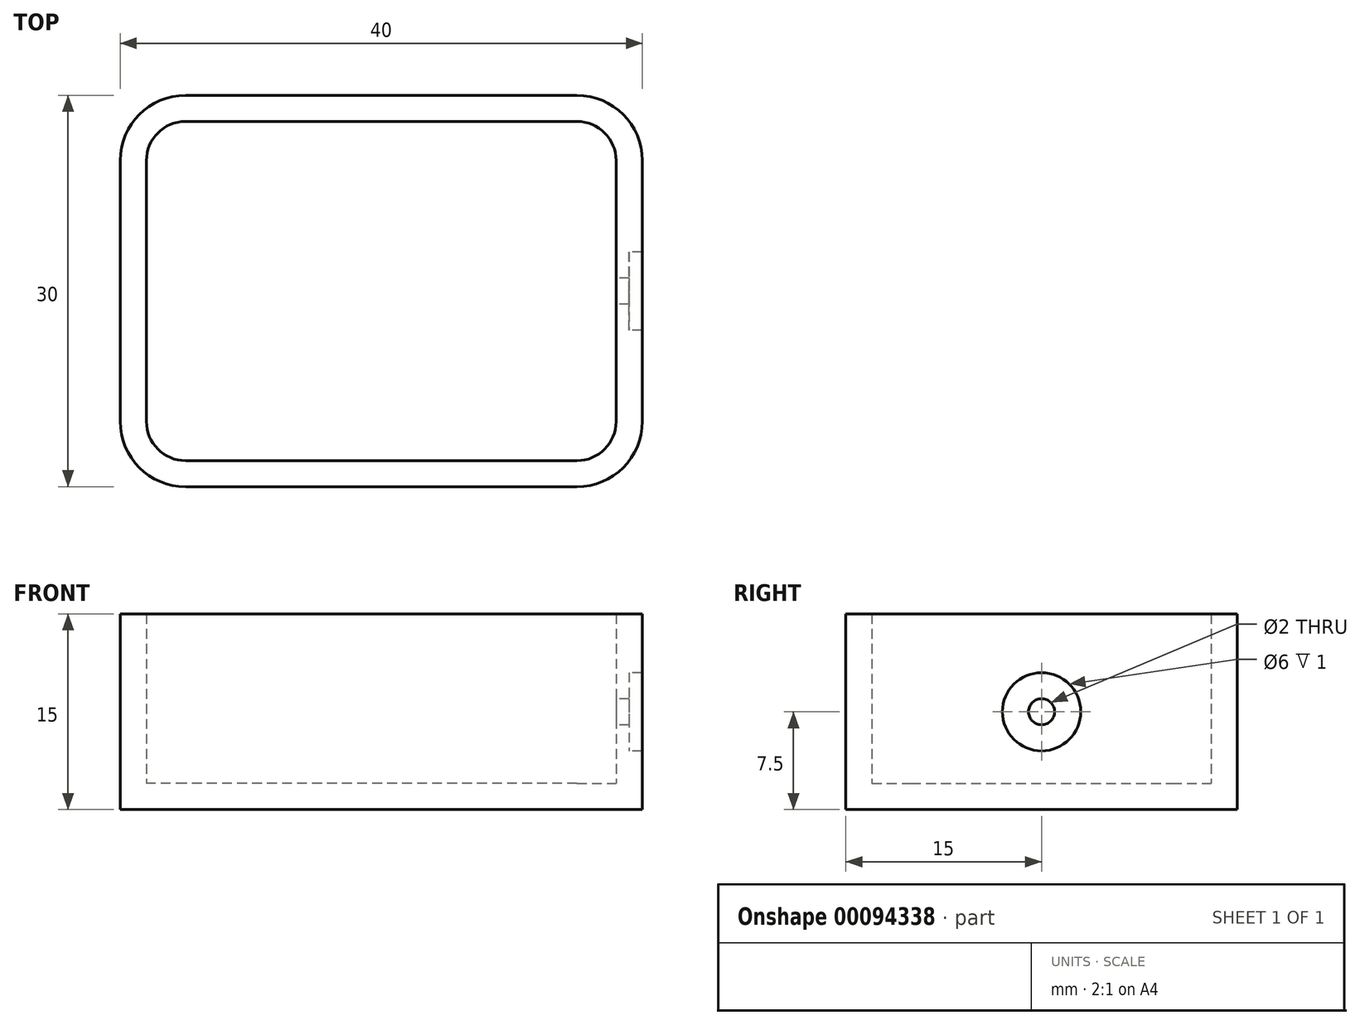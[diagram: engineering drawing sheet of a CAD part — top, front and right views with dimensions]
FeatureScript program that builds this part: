
annotation { "Feature Type Name" : "Feature", "Feature Type Description" : "" }
export const myFeature = defineFeature(function(context is Context, id is Id, definition is map)
    precondition{}
    {
        {
            var Q0;
            Q0=qCreatedBy(makeId("Top.planeOp"),FACE);
            var sketch = newSketch(context, id + "F0", { "sketchPlane" : qUnion([Q0])});
            skLineSegment(sketch, "E0.bottom", {"start": v(20, -15) * mm, "end": v(-20, -15) * mm});
            skLineSegment(sketch, "E0.top", {"start": v(20, 15) * mm, "end": v(-20, 15) * mm});
            skLineSegment(sketch, "E0.left", {"start": v(20, -15) * mm, "end": v(20, 15) * mm});
            skLineSegment(sketch, "E0.right", {"start": v(-20, -15) * mm, "end": v(-20, 15) * mm});
            skPoint(sketch, "E0.middle", {"position": v(0, 0) * mm});
            skSolve(sketch);
        }
        {
            var Q0;
            Q0=makeQuery(id+"F0.imprint","IMPRINT",FACE,{"disambiguationData":[TD([[makeQuery(id+"F0.imprint","IMPRINT",EDGE,{"derivedFrom":sQuery(id+"F0.wireOp",EDGE,"E0.bottom")}),-1.0]])]});
            extrude(context, id + "F1", {"entities" : qUnion([Q0]), "depth" : 15 * mm});
        }
        {
            var Q0;
            Q0=makeQuery(id+"F1.opExtrude","CAP_FACE",FACE,{"disambiguationData":[OSD([sQuery(id+"F0.wireOp",EDGE,"E0.bottom"),sQuery(id+"F0.wireOp",EDGE,"E0.top"),sQuery(id+"F0.wireOp",EDGE,"E0.left"),sQuery(id+"F0.wireOp",EDGE,"E0.right")])],"isStart":false});
            shell(context, id + "F2", {"entities" : qUnion([Q0]), "thickness" : 2 * mm});
        }
        {
            var Q0;
            Q0=makeQuery(id+"F1.opExtrude","SWEPT_EDGE",EDGE,{"disambiguationData":[OSD([sQuery(id+"F0.wireOp",EDGE,"E0.bottom"),sQuery(id+"F0.wireOp",EDGE,"E0.left")])]});
            var Q1;
            Q1=makeQuery(id+"F1.opExtrude","SWEPT_EDGE",EDGE,{"disambiguationData":[OSD([sQuery(id+"F0.wireOp",EDGE,"E0.top"),sQuery(id+"F0.wireOp",EDGE,"E0.left")])]});
            var Q2;
            Q2=makeQuery(id+"F1.opExtrude","SWEPT_EDGE",EDGE,{"disambiguationData":[OSD([sQuery(id+"F0.wireOp",EDGE,"E0.bottom"),sQuery(id+"F0.wireOp",EDGE,"E0.right")])]});
            var Q3;
            Q3=makeQuery(id+"F1.opExtrude","SWEPT_EDGE",EDGE,{"disambiguationData":[OSD([sQuery(id+"F0.wireOp",EDGE,"E0.top"),sQuery(id+"F0.wireOp",EDGE,"E0.right")])]});
            fillet(context, id + "F3", {"entities" : qUnion([Q0, Q1, Q2, Q3]), "radius" : 5 * mm, "tangentPropagation" : true, "allowEdgeOverflow" : false});
        }
        {
            var Q0;
            Q0=makeQuery(id+"F2.opShell","OFFSET_EDGE",EDGE,{"disambiguationData":[OSD([sQuery(id+"F0.wireOp",EDGE,"E0.top"),sQuery(id+"F0.wireOp",EDGE,"E0.right")])]});
            var Q1;
            Q1=makeQuery(id+"F2.opShell","OFFSET_EDGE",EDGE,{"disambiguationData":[OSD([sQuery(id+"F0.wireOp",EDGE,"E0.bottom"),sQuery(id+"F0.wireOp",EDGE,"E0.right")])]});
            var Q2;
            Q2=makeQuery(id+"F2.opShell","OFFSET_EDGE",EDGE,{"disambiguationData":[OSD([sQuery(id+"F0.wireOp",EDGE,"E0.top"),sQuery(id+"F0.wireOp",EDGE,"E0.left")])]});
            var Q3;
            Q3=makeQuery(id+"F2.opShell","OFFSET_EDGE",EDGE,{"disambiguationData":[OSD([sQuery(id+"F0.wireOp",EDGE,"E0.bottom"),sQuery(id+"F0.wireOp",EDGE,"E0.left")])]});
            fillet(context, id + "F4", {"entities" : qUnion([Q0, Q1, Q2, Q3]), "radius" : 3 * mm, "tangentPropagation" : true, "allowEdgeOverflow" : false});
        }
        {
            var Q0;
            Q0=makeQuery(id+"F1.opExtrude","SWEPT_FACE",FACE,{"disambiguationData":[OSD([sQuery(id+"F0.wireOp",EDGE,"E0.left")])]});
            var sketch = newSketch(context, id + "F5", { "sketchPlane" : qUnion([Q0])});
            skLineSegment(sketch, "E1.0", {"start": v(-10, 15) * mm, "end": v(-10, 0) * mm});
            skLineSegment(sketch, "E2.0", {"start": v(10, 0) * mm, "end": v(10, 15) * mm});
            skLineSegment(sketch, "E3", {"start": v(-10, 0) * mm, "end": v(10, 15) * mm});
            skPoint(sketch, "E4", {"position": v(0, 7.5) * mm});
            skSolve(sketch);
        }
        {
            var Q0;
            Q0=sQuery(id+"F5.wireOp",VERTEX,"E4");
            var Q1;
            Q1=makeQuery(id+"F1.opExtrude","SWEPT_BODY",BODY,{"disambiguationData":[OSD([sQuery(id+"F0.wireOp",EDGE,"E0.bottom"),sQuery(id+"F0.wireOp",EDGE,"E0.top"),sQuery(id+"F0.wireOp",EDGE,"E0.left"),sQuery(id+"F0.wireOp",EDGE,"E0.right")])]});
            hole(context, id + "F6", {"style" : HoleStyle.C_BORE, "endStyle" : HoleEndStyle.BLIND, "holeDiameter" : 2 * mm, "cBoreDiameter" : 6 * mm, "cBoreDepth" : 1 * mm, "holeDepth" : 12 * mm, "locations" : qUnion([Q0]), "scope" : qUnion([Q1]), "startStyle" : HoleStartStyle.SKETCH});
        }
    });
